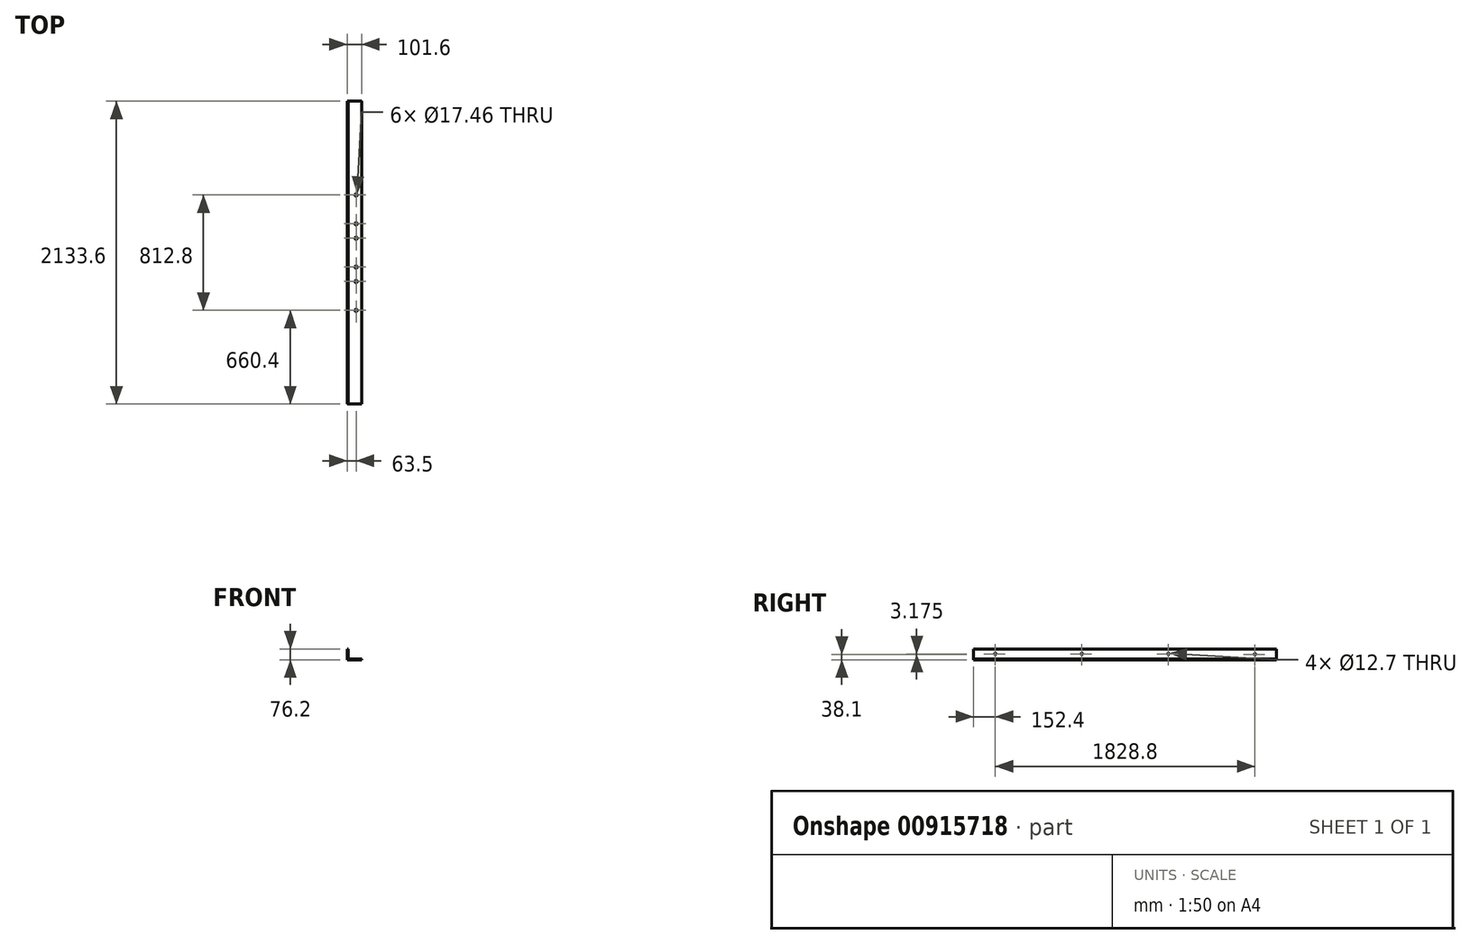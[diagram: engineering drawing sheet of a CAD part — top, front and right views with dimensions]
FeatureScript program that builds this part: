
annotation { "Feature Type Name" : "Feature", "Feature Type Description" : "" }
export const myFeature = defineFeature(function(context is Context, id is Id, definition is map)
    precondition{}
    {
        {
            var Q0;
            Q0=qCreatedBy(makeId("Front.planeOp"),FACE);
            var sketch = newSketch(context, id + "F0", { "sketchPlane" : qUnion([Q0])});
            skLineSegment(sketch, "E0", {"start": v(0, 76.2) * mm, "end": v(0, 0) * mm});
            skLineSegment(sketch, "E1", {"start": v(0, 0) * mm, "end": v(101.6, 0) * mm});
            skLineSegment(sketch, "E2", {"start": v(101.6, 0) * mm, "end": v(101.6, 3.17) * mm});
            skLineSegment(sketch, "E3", {"start": v(98.43, 6.35) * mm, "end": v(9.52, 6.35) * mm});
            skLineSegment(sketch, "E4", {"start": v(6.35, 9.52) * mm, "end": v(6.35, 73.03) * mm});
            skLineSegment(sketch, "E5", {"start": v(3.17, 76.2) * mm, "end": v(0, 76.2) * mm});
            skPoint(sketch, "E6.visualSharp", {"position": v(6.35, 6.35) * mm});
            skArc(sketch, "E6.filletArc", {"start": v(6.35, 9.52) * mm, "mid": v(7.28, 7.28) * mm, "end": v(9.52, 6.35) * mm});
            skPoint(sketch, "E7.visualSharp", {"position": v(6.35, 76.2) * mm});
            skArc(sketch, "E7.filletArc", {"start": v(6.35, 73.03) * mm, "mid": v(5.42, 75.27) * mm, "end": v(3.17, 76.2) * mm});
            skPoint(sketch, "E8.visualSharp", {"position": v(101.6, 6.35) * mm});
            skArc(sketch, "E8.filletArc", {"start": v(101.6, 3.17) * mm, "mid": v(100.67, 5.42) * mm, "end": v(98.43, 6.35) * mm});
            skSolve(sketch);
        }
        {
            var Q0;
            Q0=qSketchRegion(id+"F0",true);
            extrude(context, id + "F1", {"entities" : qUnion([Q0]), "depth" : 2133.6 * mm, "offsetDistance" : 25.4 * mm, "symmetric" : true});
        }
        {
            var Q0;
            Q0=makeQuery(id+"F1.opExtrude","SWEPT_FACE",FACE,{"disambiguationData":[OSD([sQuery(id+"F0.wireOp",EDGE,"E1")])]});
            var sketch = newSketch(context, id + "F2", { "sketchPlane" : qUnion([Q0])});
            skCircle(sketch, "E9", {"center": v(63.5, -203.2) * mm, "radius": 8.73 * mm});
            skCircle(sketch, "E10", {"center": v(63.5, -406.4) * mm, "radius": 8.73 * mm});
            skLineSegment(sketch, "E11", {"start": v(0, 0) * mm, "end": v(101.6, 0) * mm, "construction": true});
            skCircle(sketch, "E12", {"center": v(63.5, -101.6) * mm, "radius": 8.73 * mm});
            skCircle(sketch, "E13", {"center": v(63.5, 101.6) * mm, "radius": 8.73 * mm});
            skCircle(sketch, "E14", {"center": v(63.5, 203.2) * mm, "radius": 8.73 * mm});
            skCircle(sketch, "E15", {"center": v(63.5, 406.4) * mm, "radius": 8.73 * mm});
            skSolve(sketch);
        }
        {
            var Q0;
            Q0=qSketchRegion(id+"F2",true);
            extrude(context, id + "F3", {"entities" : qUnion([Q0]), "operationType" : NewBodyOperationType.REMOVE, "endBound" : BoundingType.THROUGH_ALL, "oppositeDirection" : true, "depth" : 25.4 * mm, "offsetDistance" : 25.4 * mm});
        }
        {
            var Q0;
            Q0=makeQuery(id+"F1.opExtrude","SWEPT_FACE",FACE,{"disambiguationData":[OSD([sQuery(id+"F0.wireOp",EDGE,"E0")])]});
            var sketch = newSketch(context, id + "F4", { "sketchPlane" : qUnion([Q0])});
            skCircle(sketch, "E16", {"center": v(-304.8, 41.27) * mm, "radius": 6.35 * mm});
            skCircle(sketch, "E17", {"center": v(304.8, 41.27) * mm, "radius": 6.35 * mm});
            skCircle(sketch, "E18", {"center": v(-914.4, 38.1) * mm, "radius": 6.35 * mm});
            skCircle(sketch, "E19", {"center": v(914.4, 41.28) * mm, "radius": 6.35 * mm});
            skSolve(sketch);
        }
        {
            var Q0;
            Q0=qSketchRegion(id+"F4",true);
            extrude(context, id + "F5", {"entities" : qUnion([Q0]), "operationType" : NewBodyOperationType.REMOVE, "endBound" : BoundingType.THROUGH_ALL, "oppositeDirection" : true, "depth" : 25.4 * mm, "offsetDistance" : 25.4 * mm});
        }
    });
